# Revit family: FU_Chair_Sandler_OSWELL 1-2PP
name_source: partatom
category: Furniture
units: mm (PartAtom-declared; Revit-internal decimal feet)

## family parameters
Always vertical = Yes
Cut with Voids When Loaded = No
OmniClass Number = 23.40.20.00
OmniClass Title = General Furniture and Specialties
Render Appearance Source = Family Geometry
Room Calculation Point = No
Shared = No
Work Plane-Based = No

## types (1)
- Oswell 1.2PP
    Default Elevation = 0 mm  [stored 0 ft]
    Depth = 545 mm  [stored 1.78806 ft]
    Description = Stacking side chair made of ridged polypropylene with a non-slip texture. Steel legs. One-third of the materials are recycled, and the chair is Greenguard Gold-certified to have a minimal impact on indoor air quality.
    Height = 815 mm  [stored 2.67388 ft]
    Manufacturer = Sandler
    Model = Oswell 1.2PP
    URL = https://www.sandlerseating.com
    Width = 520 mm  [stored 1.70604 ft]

note: [stored X ft] marks values corroborated as IEEE doubles in the binary element streams (Revit-internal decimal feet)

## geometry (parser evidence)
native form markers: Sweep x7
no freeform markers — native parametric forms only
